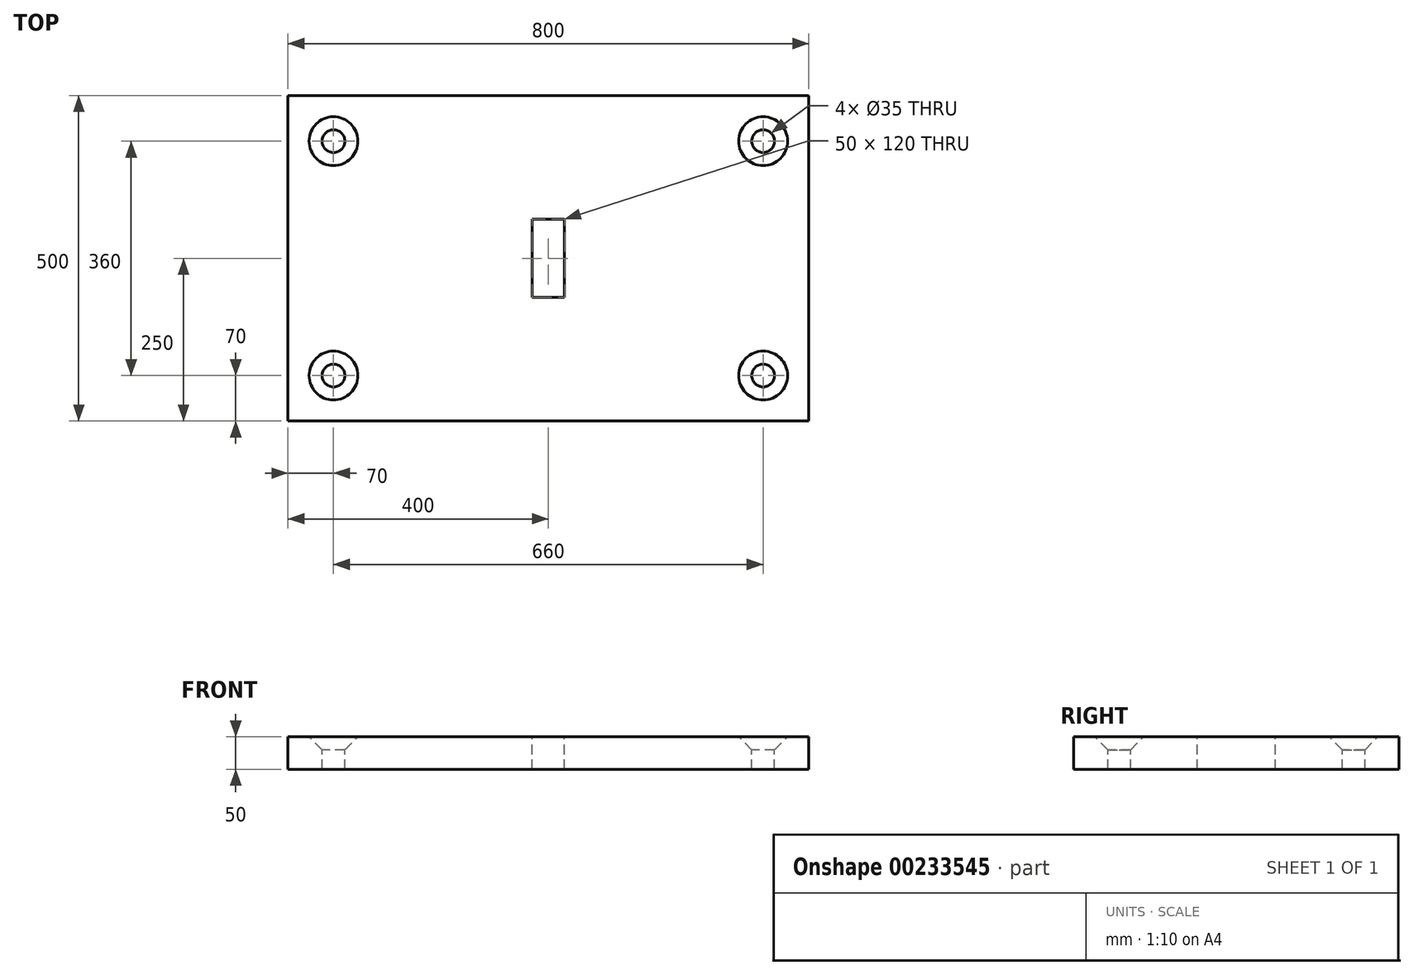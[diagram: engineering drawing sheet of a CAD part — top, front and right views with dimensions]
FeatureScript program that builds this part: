
annotation { "Feature Type Name" : "Feature", "Feature Type Description" : "" }
export const myFeature = defineFeature(function(context is Context, id is Id, definition is map)
    precondition{}
    {
        {
            var Q0;
            Q0=qCreatedBy(makeId("Top.planeOp"),FACE);
            var sketch = newSketch(context, id + "F0", { "sketchPlane" : qUnion([Q0])});
            skLineSegment(sketch, "E0.bottom", {"start": v(400, 250) * mm, "end": v(-400, 250) * mm});
            skLineSegment(sketch, "E0.top", {"start": v(400, -250) * mm, "end": v(-400, -250) * mm});
            skLineSegment(sketch, "E0.left", {"start": v(400, 250) * mm, "end": v(400, -250) * mm});
            skLineSegment(sketch, "E0.right", {"start": v(-400, 250) * mm, "end": v(-400, -250) * mm});
            skPoint(sketch, "E0.middle", {"position": v(0, 0) * mm});
            skCircle(sketch, "E1", {"center": v(-330, -180) * mm, "radius": 17.5 * mm});
            skLineSegment(sketch, "E2.bottom", {"start": v(25, 60) * mm, "end": v(-25, 60) * mm});
            skLineSegment(sketch, "E2.top", {"start": v(25, -60) * mm, "end": v(-25, -60) * mm});
            skLineSegment(sketch, "E2.left", {"start": v(25, 60) * mm, "end": v(25, -60) * mm});
            skLineSegment(sketch, "E2.right", {"start": v(-25, 60) * mm, "end": v(-25, -60) * mm});
            skCircle(sketch, "E3.0.1.0", {"center": v(-330, 180) * mm, "radius": 17.5 * mm});
            skCircle(sketch, "E3.1.0.0", {"center": v(330, -180) * mm, "radius": 17.5 * mm});
            skCircle(sketch, "E3.1.1.0", {"center": v(330, 180) * mm, "radius": 17.5 * mm});
            skCircle(sketch, "E3.2.0.0", {"center": v(990, -180) * mm, "radius": 17.5 * mm});
            skCircle(sketch, "E3.2.1.0", {"center": v(990, 180) * mm, "radius": 17.5 * mm});
            skLineSegment(sketch, "E3.direction1", {"start": v(-330, -180) * mm, "end": v(330, -180) * mm, "construction": true});
            skLineSegment(sketch, "E3.direction2", {"start": v(-330, -180) * mm, "end": v(-330, 180) * mm, "construction": true});
            skSolve(sketch);
        }
        {
            var Q0;
            Q0=makeQuery(id+"F0.imprint","IMPRINT",FACE,{"disambiguationData":[TD([[makeQuery(id+"F0.imprint","IMPRINT",EDGE,{"derivedFrom":sQuery(id+"F0.wireOp",EDGE,"E0.bottom")}),1.0]])]});
            var Q1;
            Q1=makeQuery(id+"F0.imprint","IMPRINT",FACE,{"disambiguationData":[TD([[makeQuery(id+"F0.imprint","IMPRINT",EDGE,{"derivedFrom":sQuery(id+"F0.wireOp",EDGE,"E1")}),1.0]])]});
            var Q2;
            Q2=makeQuery(id+"F0.imprint","IMPRINT",FACE,{"disambiguationData":[TD([[makeQuery(id+"F0.imprint","IMPRINT",EDGE,{"derivedFrom":sQuery(id+"F0.wireOp",EDGE,"E3.0.1.0")}),1.0]])]});
            var Q3;
            Q3=makeQuery(id+"F0.imprint","IMPRINT",FACE,{"disambiguationData":[TD([[makeQuery(id+"F0.imprint","IMPRINT",EDGE,{"derivedFrom":sQuery(id+"F0.wireOp",EDGE,"E3.1.1.0")}),1.0]])]});
            var Q4;
            Q4=makeQuery(id+"F0.imprint","IMPRINT",FACE,{"disambiguationData":[TD([[makeQuery(id+"F0.imprint","IMPRINT",EDGE,{"derivedFrom":sQuery(id+"F0.wireOp",EDGE,"E3.1.0.0")}),1.0]])]});
            extrude(context, id + "F1", {"entities" : qUnion([Q0, Q1, Q2, Q3, Q4]), "oppositeDirection" : true, "depth" : 50 * mm});
        }
        {
            var Q0;
            Q0=sQuery(id+"F0.wireOp",VERTEX,"E3.direction1.start");
            var Q1;
            Q1=sQuery(id+"F0.wireOp",VERTEX,"E3.0.1.0.center");
            var Q2;
            Q2=sQuery(id+"F0.wireOp",VERTEX,"E3.1.1.0.center");
            var Q3;
            Q3=sQuery(id+"F0.wireOp",VERTEX,"E3.1.0.0.center");
            var Q4;
            Q4=makeQuery(id+"F1.opExtrude","SWEPT_BODY",BODY,{"disambiguationData":[OSD([sQuery(id+"F0.wireOp",EDGE,"E0.bottom"),sQuery(id+"F0.wireOp",EDGE,"E0.top"),sQuery(id+"F0.wireOp",EDGE,"E0.left"),sQuery(id+"F0.wireOp",EDGE,"E0.right"),sQuery(id+"F0.wireOp",EDGE,"E2.bottom"),sQuery(id+"F0.wireOp",EDGE,"E2.top"),sQuery(id+"F0.wireOp",EDGE,"E2.left"),sQuery(id+"F0.wireOp",EDGE,"E2.right")])]});
            hole(context, id + "F2", {"style" : HoleStyle.C_SINK, "endStyle" : HoleEndStyle.THROUGH, "holeDiameter" : 35 * mm, "cSinkDiameter" : 75 * mm, "cSinkAngle" : 90 * degree, "startFromSketch" : true, "locations" : qUnion([Q0, Q1, Q2, Q3]), "scope" : qUnion([Q4]), "isTappedThrough" : true});
        }
    });
